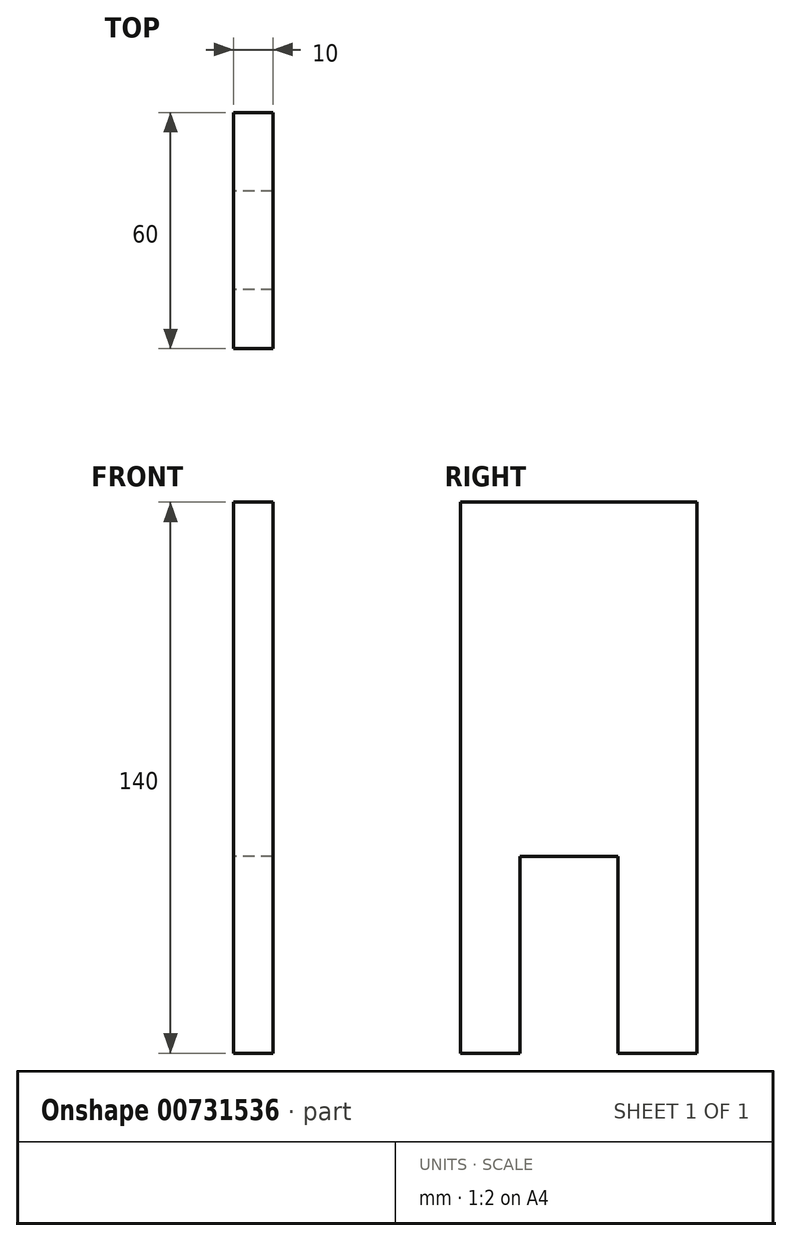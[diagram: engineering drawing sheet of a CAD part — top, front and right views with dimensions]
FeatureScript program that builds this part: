
annotation { "Feature Type Name" : "Feature", "Feature Type Description" : "" }
export const myFeature = defineFeature(function(context is Context, id is Id, definition is map)
    precondition{}
    {
        {
            var Q0;
            Q0=qCreatedBy(makeId("Right.planeOp"),FACE);
            var sketch = newSketch(context, id + "F0", { "sketchPlane" : qUnion([Q0])});
            skLineSegment(sketch, "E0.bottom", {"start": v(0, 0) * mm, "end": v(60, 0) * mm});
            skLineSegment(sketch, "E0.top", {"start": v(0, 140) * mm, "end": v(60, 140) * mm});
            skLineSegment(sketch, "E0.left", {"start": v(0, 0) * mm, "end": v(0, 140) * mm});
            skLineSegment(sketch, "E0.right", {"start": v(60, 0) * mm, "end": v(60, 140) * mm});
            skLineSegment(sketch, "E1.bottom", {"start": v(15, 0) * mm, "end": v(40, 0) * mm});
            skLineSegment(sketch, "E1.top", {"start": v(15, 50) * mm, "end": v(40, 50) * mm});
            skLineSegment(sketch, "E1.left", {"start": v(15, 0) * mm, "end": v(15, 50) * mm});
            skLineSegment(sketch, "E1.right", {"start": v(40, 0) * mm, "end": v(40, 50) * mm});
            skSolve(sketch);
        }
        {
            var Q0;
            Q0=makeQuery(id+"F0.imprint","IMPRINT",FACE,{"disambiguationData":[TD([[makeQuery(id+"F0.imprint","IMPRINT",EDGE,{"derivedFrom":sQuery(id+"F0.wireOp",EDGE,"E0.top")}),-1.0]])]});
            extrude(context, id + "F1", {"entities" : qUnion([Q0]), "depth" : 10 * mm, "offsetDistance" : 25 * mm});
        }
    });
